FCSTD DOCUMENT  (FreeCAD 0.20R29177 (Git))
Label: DonneesBoitier
License: All rights reserved
LicenseURL: http://en.wikipedia.org/wiki/All_rights_reserved
objects: Spreadsheet::Sheet×1

FEATURE [Spreadsheet::Sheet] Spreadsheet
  cells = A1=Angle; B1(xxAngle)=60; A2=LargEconche; B2(xxLargEconche)=15; A3=LongBase; B3(xxLongBase)=200; C3=Longeur de la base de l'enssemble , joue sur les angles et longeur de face Ar; A4=DiametreEcrou; B4(xxDiametreEcrou)=8; A5=AxeEncochesFaceAv; B5(xxAxeEncochesFaceAv)=10; C5=largeur de chaque cotés de l'ecran; D5=Sert à l'axe vertical du centre des trous et encoches en face AV; A6=LargeurEncasEcran; B6(xxLargeurEncasEcran)=100; C6=Largeur encastrement ecran; D6=100; A7=HauteurEncasEcran; B7(xxHauteurEncasEcran)=165; C7=Hauteur encastrement ecran; D7=165; A8=EpFaceAvAR; B8(xxEpFaceAvAr)=5; C8=Epaisseur Face Av AR; A9=EpEcrou; B9(xxEpEcrou)=4; C9=Epaisseur pour l'encastrement des ecrous; A10=DistEcrou; B10(xxDistEcrou)=5; C10=Distance d'encastrement de l'ecrou; A11=DiamVis; B11(xxDiamVis)=5; A12=LongVis; B12(xxLongVis)=12; A13=DiametreTrou; B13(xxDiametreTrou)==xxDiamVis * 1.05; C13=DiamVis + Marge 5%; A14=LargeurExtEcran; B14(xxLargeurExtEcran)=; C14=Largeur Externe de l'ecran; D14=110; A15=HauteurExtEcran; B15(xxHauteurExtEcran)=; C15=Hauteur Externe de l'ecran/ sert aussi pour la partie Ar rectiligne; D15=193; A16=RebordAvAr; B16(xxRebordAvAr)=10; C16=Rebord face Av et Ar par rapport au corp; D16=RebordAVAr+EpFaceAvAr/2 doit etre le centre de l'axe vertical sur lesquels sont centrés les trous et les encoches en facade; A17=FaEspaceHaut; B17(xxFaEspaceHaut)=35; C17=Espace entre le haut de la FA et le haut de l'ecran; A18=RapportHautEcranSurLarg; B18(xxRapportHautEcranSurLarg)=; C18=Pour garder un proportion du support; D18=xxHauteurExtEcran / xxLargeurExtEcran; A19=Hauteur; B19(xxHauteur)=338.63; C19=Hauteur Face AV; D19=xxHauteurExtEcran * xxRapportHautEcranSurLarg; A20=Largeur; B20(xxlargeur)=160; C20=Largeur Face AV et AR 140 ecran encastrable AV ; D20=xxLargeurExtEcran + 2 * xxBordEcranFaceAv; A21=EpEncoche; B21(xxEpEncoche)==xxEpFaceAvAr; C21=egal epaisseur face AvAr; A22=HautEncocheFemelle; B22(xxHautEncocheFemelle)==xxEpEncoche; C22=EpEncoche + Marge si necessaire; D22=?? Hauteur encoche femelle; E22=xxEpTrou; A23=LargEncocheFemelle; B23(xxLargEncocheFemelle)==xxLargEconche; C23=LargEconche + Marge si necessaire; D23=?? Largeur encoche femelle; E23=xxLargTrou; A24=LongEncoches; B24(xxLongEncoches)==xxEpFaceAvAr; C24=egal epaisseur face AvAr; A25=RayonCongé; B25(xxRayonConge)=10; A26=LargLatHaut; B26(xxLargLatHaut)=65; C26=Largeur laterale et Largeur dessus totale sans encoche; A27=LongDessus; B27(xxLongDessus)==xxlargeur - 2 * xxAxeEncochesFaceAv - xxLongEncoches; A28=LongeurDecoupe; B28(xxLongeurDecoupe)=30; A29=LargeurDecoupe; B29(xxLargeurDecoupe)=2; A30=EspaceDecoupe; B30(xxEspaceDecoupe)=4; A31=SautLigneDecoupe; B31(xxSautLigneDecoupe)=3; A34=ArHautPartieHaute; B34(xxArHautPartieHaute)==xxHauteurEncasEcran; C34=Haute de la partie Ar non flexible; A35=Face Ar; A36=HauteurAr; B36(xxHauteurAr)==72.59999999999999 + 130.8 + 60 + 27.5 + xxRebordAvAr; C36=Mesure du coté dans Curve avec (I) + xxRebordAvAr; A37=EspaceDebutCourbe; B37(xxEspaceDebutCourbe)=15; C37=Espace haut (  par rapport encoche)et bas du début et fin de la courbe mesuré sur proto; A38=EspaceFinCourbe; B38(xxEspaceFinCourbe)==xxEspaceDebutCourbe / 2; A39=DecoupeHauteur; B39(xxDecoupeHauteur)=128; C39=Mesure sur lignes de construction
